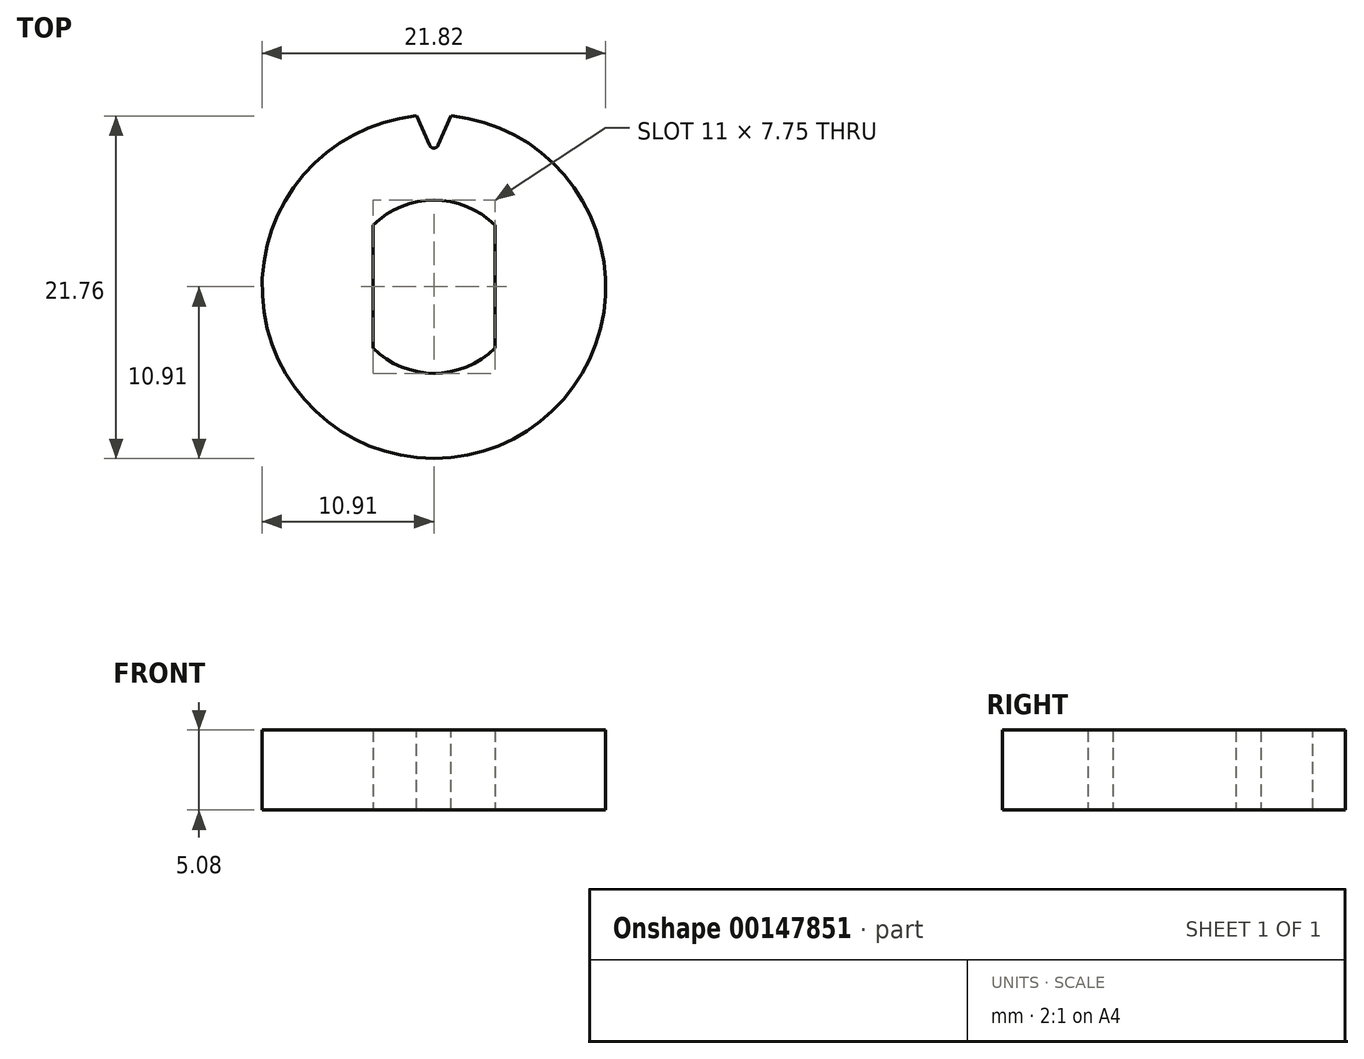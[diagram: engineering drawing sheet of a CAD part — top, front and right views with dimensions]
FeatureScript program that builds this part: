
annotation { "Feature Type Name" : "Feature", "Feature Type Description" : "" }
export const myFeature = defineFeature(function(context is Context, id is Id, definition is map)
    precondition{}
    {
        {
            var Q0;
            Q0=qCreatedBy(makeId("Top.planeOp"),FACE);
            var sketch = newSketch(context, id + "F0", { "sketchPlane" : qUnion([Q0])});
            skLineSegment(sketch, "E0.bottom", {"start": v(-3.87, -3.9) * mm, "end": v(3.87, -3.9) * mm, "construction": true});
            skLineSegment(sketch, "E0.top", {"start": v(-3.87, 3.9) * mm, "end": v(3.87, 3.9) * mm, "construction": true});
            skLineSegment(sketch, "E0.left", {"start": v(-3.87, -3.9) * mm, "end": v(-3.87, 3.9) * mm});
            skLineSegment(sketch, "E0.right", {"start": v(3.87, -3.9) * mm, "end": v(3.87, 3.9) * mm});
            skPoint(sketch, "E0.middle", {"position": v(0, 0) * mm});
            skArc(sketch, "E1", {"start": v(3.87, 3.9) * mm, "mid": v(0, 5.5) * mm, "end": v(-3.87, 3.9) * mm});
            skArc(sketch, "E2", {"start": v(-3.87, -3.9) * mm, "mid": v(0, -5.5) * mm, "end": v(3.87, -3.9) * mm});
            skCircle(sketch, "E3", {"center": v(0, 0) * mm, "radius": 10.9 * mm});
            skSolve(sketch);
        }
        {
            var Q0;
            Q0=makeQuery(id+"F0.imprint","IMPRINT",FACE,{"disambiguationData":[TD([[makeQuery(id+"F0.imprint","IMPRINT",EDGE,{"derivedFrom":sQuery(id+"F0.wireOp",EDGE,"E0.left")}),1.0]])]});
            extrude(context, id + "F1", {"entities" : qUnion([Q0]), "depth" : 5.08 * mm});
        }
        {
            var Q0;
            Q0=makeQuery(id+"F1.opExtrude","CAP_FACE",FACE,{"disambiguationData":[OSD([sQuery(id+"F0.wireOp",EDGE,"E0.left"),sQuery(id+"F0.wireOp",EDGE,"E0.right"),sQuery(id+"F0.wireOp",EDGE,"E1"),sQuery(id+"F0.wireOp",EDGE,"E2"),sQuery(id+"F0.wireOp",EDGE,"E3")])],"isStart":false});
            var sketch = newSketch(context, id + "F2", { "sketchPlane" : qUnion([Q0])});
            skLineSegment(sketch, "E4", {"start": v(0, 0) * mm, "end": v(0, 10.9) * mm, "construction": true});
            skLineSegment(sketch, "E5", {"start": v(0, 0) * mm, "end": v(0.75, 10.88) * mm, "construction": true});
            skArc(sketch, "E6", {"start": v(1.1, 10.85) * mm, "mid": v(0, 10.9) * mm, "end": v(-1.1, 10.85) * mm});
            skLineSegment(sketch, "E7", {"start": v(-1.1, 10.85) * mm, "end": v(-0.27, 8.98) * mm});
            skLineSegment(sketch, "E8", {"start": v(1.1, 10.85) * mm, "end": v(0.27, 8.98) * mm});
            skPoint(sketch, "E9", {"position": v(0.69, 9.92) * mm});
            skArc(sketch, "E10", {"start": v(-0.27, 8.98) * mm, "mid": v(0, 8.8) * mm, "end": v(0.27, 8.98) * mm});
            skSolve(sketch);
        }
        {
            var Q0;
            Q0=qSketchRegion(id+"F2",true);
            var Q1;
            Q1=makeQuery(id+"F1.opExtrude","CAP_FACE",FACE,{"disambiguationData":[OSD([sQuery(id+"F0.wireOp",EDGE,"E0.left"),sQuery(id+"F0.wireOp",EDGE,"E0.right"),sQuery(id+"F0.wireOp",EDGE,"E1"),sQuery(id+"F0.wireOp",EDGE,"E2"),sQuery(id+"F0.wireOp",EDGE,"E3")])],"isStart":true});
            extrude(context, id + "F3", {"entities" : qUnion([Q0]), "operationType" : NewBodyOperationType.REMOVE, "endBound" : BoundingType.UP_TO_SURFACE, "oppositeDirection" : true, "endBoundEntityFace" : qUnion([Q1]), "depth" : 25.4 * mm});
        }
    });
